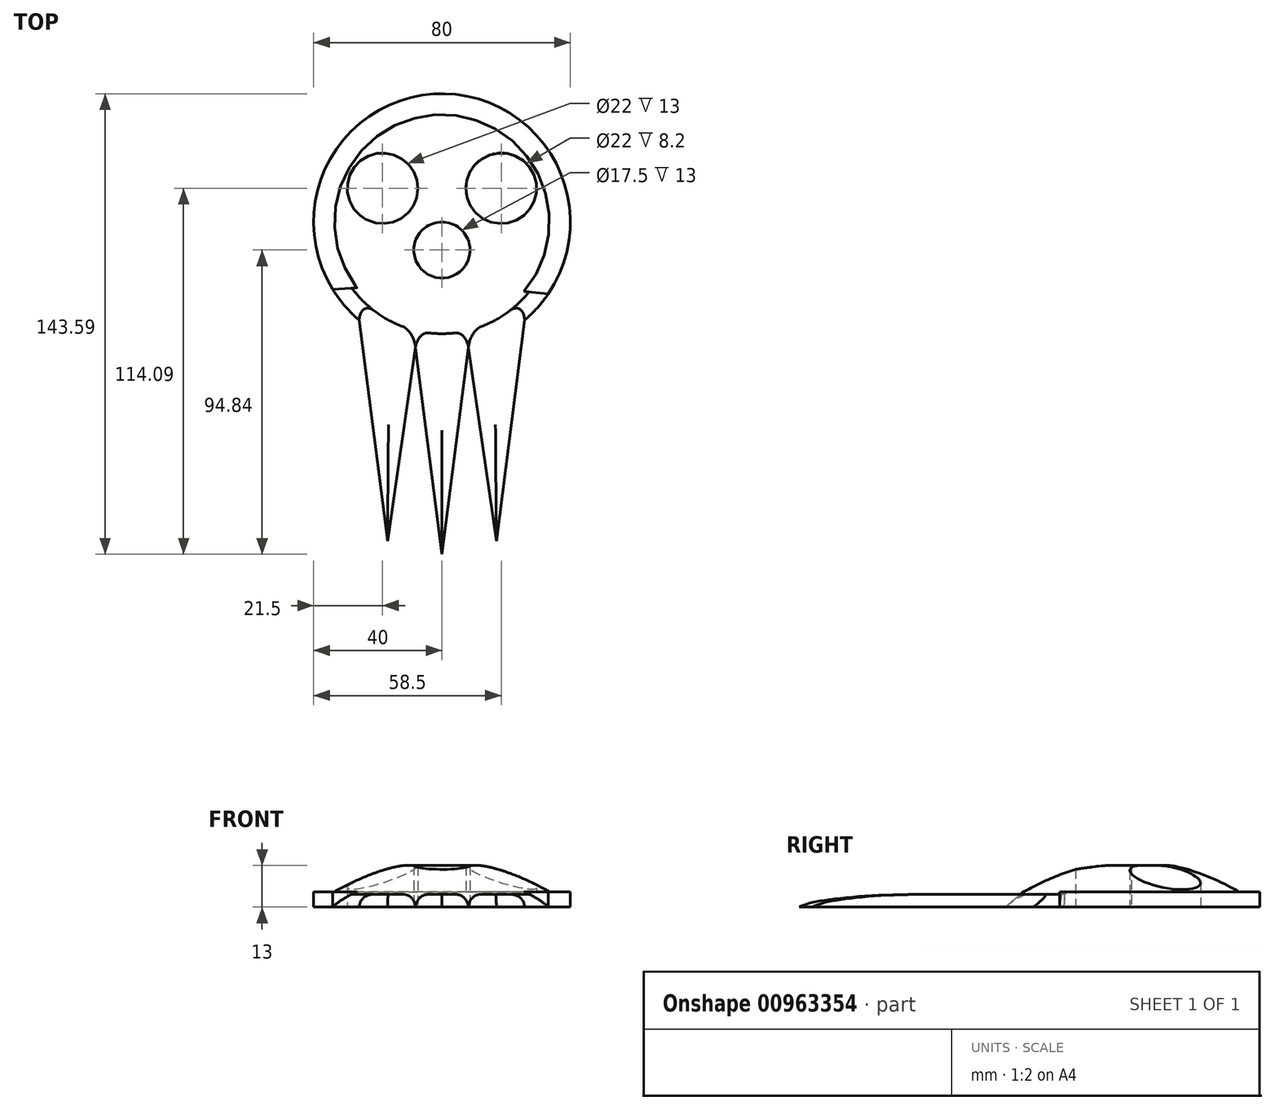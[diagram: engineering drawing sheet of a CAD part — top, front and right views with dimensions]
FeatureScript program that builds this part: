
annotation { "Feature Type Name" : "Feature", "Feature Type Description" : "" }
export const myFeature = defineFeature(function(context is Context, id is Id, definition is map)
    precondition{}
    {
        {
            var Q0;
            Q0=qCreatedBy(makeId("Top.planeOp"),FACE);
            var sketch = newSketch(context, id + "F0", { "sketchPlane" : qUnion([Q0])});
            skCircle(sketch, "E0", {"center": v(0, 0) * mm, "radius": 40 * mm});
            skLineSegment(sketch, "E1", {"start": v(0, 0) * mm, "end": v(18.5, 0) * mm});
            skLineSegment(sketch, "E2", {"start": v(18.5, 0) * mm, "end": v(18.5, 10.5) * mm});
            skCircle(sketch, "E3", {"center": v(18.5, 10.5) * mm, "radius": 11 * mm});
            skLineSegment(sketch, "E4", {"start": v(0, 0) * mm, "end": v(0, -8.75) * mm});
            skCircle(sketch, "E5", {"center": v(0, -8.75) * mm, "radius": 8.75 * mm});
            skLineSegment(sketch, "E6", {"start": v(0, 0) * mm, "end": v(0, -103.59) * mm});
            skCircle(sketch, "E7.MirrorC", {"center": v(-18.5, 10.5) * mm, "radius": 11 * mm});
            skLineSegment(sketch, "E8.MirrorCS", {"start": v(-18.5, 0) * mm, "end": v(-18.5, 10.5) * mm});
            skLineSegment(sketch, "E9.MirrorCS", {"start": v(0, 0) * mm, "end": v(-18.5, 0) * mm});
            skLineSegment(sketch, "E10", {"start": v(0, -103.59) * mm, "end": v(8.25, -39.14) * mm});
            skLineSegment(sketch, "E11", {"start": v(8.25, -39.14) * mm, "end": v(16.97, -99.51) * mm});
            skLineSegment(sketch, "E12", {"start": v(16.97, -99.51) * mm, "end": v(25.79, -30.58) * mm});
            skLineSegment(sketch, "E13.MirrorCS", {"start": v(0, -103.59) * mm, "end": v(-8.25, -39.14) * mm});
            skLineSegment(sketch, "E14.MirrorCS", {"start": v(-8.25, -39.14) * mm, "end": v(-16.97, -99.51) * mm});
            skLineSegment(sketch, "E15.MirrorCS", {"start": v(-16.97, -99.51) * mm, "end": v(-25.79, -30.58) * mm});
            skLineSegment(sketch, "E16", {"start": v(-34.05, -20.98) * mm, "end": v(0, -19.1) * mm});
            skLineSegment(sketch, "E17", {"start": v(0, -19.1) * mm, "end": v(33.14, -22.4) * mm});
            skSolve(sketch);
        }
        {
            var Q0;
            Q0=makeQuery(id+"F0.imprint","IMPRINT",FACE,{"disambiguationData":[TD([[makeQuery(id+"F0.imprint","IMPRINT",EDGE,{"derivedFrom":sQuery(id+"F0.wireOp",EDGE,"E3")}),-1.0]])]});
            var Q1;
            {var subQ2=sQuery(id+"F0.wireOp",EDGE,"CDw8CHMi-SPtq-gRNy-25xt-xmdggRBoIwYT");Q1=makeQuery(id+"F0.imprint","IMPRINT",FACE,{"disambiguationData":[TD([[makeQuery(id+"F0.imprint","IMPRINT",EDGE,{"derivedFrom":subQ2}),1.0]])]});}
            var Q2;
            {var subQ4=sQuery(id+"F0.wireOp",EDGE,"HV52Obsy-qp4e-FB5j-iO7Q-z4RWAlnaYpS9");Q2=makeQuery(id+"F0.imprint","IMPRINT",FACE,{"disambiguationData":[TD([[makeQuery(id+"F0.imprint","IMPRINT",EDGE,{"derivedFrom":subQ4}),1.0]])]});}
            var Q3;
            {var subQ0=sQuery(id+"F0.wireOp",EDGE,"E16");Q3=makeQuery(id+"F0.imprint","IMPRINT",FACE,{"disambiguationData":[TD([[makeQuery(id+"F0.imprint","IMPRINT",EDGE,{"derivedFrom":subQ0}),-1.0]])]});}
            var Q4;
            {var subQ0=sQuery(id+"F0.wireOp",EDGE,"E17");Q4=makeQuery(id+"F0.imprint","IMPRINT",FACE,{"disambiguationData":[TD([[makeQuery(id+"F0.imprint","IMPRINT",EDGE,{"derivedFrom":subQ0}),-1.0]])]});}
            extrude(context, id + "F1", {"entities" : qUnion([Q0, Q1, Q2, Q3, Q4]), "depth" : 13 * mm, "offsetDistance" : 25 * mm});
        }
        {
            var Q0;
            Q0=makeQuery(id+"F1.opExtrude","CAP_EDGE",EDGE,{"disambiguationData":[OSD([sQuery(id+"F0.wireOp",EDGE,"E0")])],"isStart":false});
            fillet(context, id + "F2", {"entities" : qUnion([Q0]), "radius" : 39 * mm, "tangentPropagation" : true, "rho" : 0.3, "crossSection" : FilletCrossSection.CONIC, "allowEdgeOverflow" : false});
        }
        {
            var Q0;
            Q0=makeQuery(id+"F0.imprint","IMPRINT",FACE,{"disambiguationData":[TD([[makeQuery(id+"F0.imprint","IMPRINT",EDGE,{"derivedFrom":sQuery(id+"F0.wireOp",EDGE,"E3")}),1.0]])]});
            var Q1;
            {var subQ0=sQuery(id+"F0.wireOp",EDGE,"E6");var subQ4=makeQuery(id+"F0.imprint","IMPRINT",VERTEX,{"derivedFrom":subQ0});Q1=makeQuery(id+"F0.imprint","IMPRINT",FACE,{"disambiguationData":[TD([[makeQuery(id+"F0.imprint","IMPRINT",EDGE,{"disambiguationData":[TD([[subQ4,1.0]])],"derivedFrom":subQ0}),1.0]])]});}
            var Q2;
            {var subQ0=sQuery(id+"F0.wireOp",EDGE,"E6");var subQ4=makeQuery(id+"F0.imprint","IMPRINT",VERTEX,{"derivedFrom":subQ0});Q2=makeQuery(id+"F0.imprint","IMPRINT",FACE,{"disambiguationData":[TD([[makeQuery(id+"F0.imprint","IMPRINT",EDGE,{"disambiguationData":[TD([[subQ4,1.0]])],"derivedFrom":subQ0}),-1.0]])]});}
            var Q3;
            Q3=makeQuery(id+"F0.imprint","IMPRINT",FACE,{"disambiguationData":[TD([[makeQuery(id+"F0.imprint","IMPRINT",EDGE,{"derivedFrom":sQuery(id+"F0.wireOp",EDGE,"E7.MirrorC")}),-1.0]])]});
            extrude(context, id + "F3", {"entities" : qUnion([Q0, Q1, Q2, Q3]), "operationType" : NewBodyOperationType.ADD, "depth" : 4.8 * mm, "offsetDistance" : 25 * mm});
        }
        {
            var Q0;
            {var subQ0=sQuery(id+"F0.wireOp",EDGE,"E14.MirrorCS");Q0=makeQuery(id+"F0.imprint","IMPRINT",FACE,{"disambiguationData":[TD([[makeQuery(id+"F0.imprint","IMPRINT",EDGE,{"derivedFrom":subQ0}),-1.0]])]});}
            var Q1;
            {var subQ0=sQuery(id+"F0.wireOp",EDGE,"E13.MirrorCS");Q1=makeQuery(id+"F0.imprint","IMPRINT",FACE,{"disambiguationData":[TD([[makeQuery(id+"F0.imprint","IMPRINT",EDGE,{"derivedFrom":subQ0}),-1.0]])]});}
            var Q2;
            {var subQ0=sQuery(id+"F0.wireOp",EDGE,"E10");Q2=makeQuery(id+"F0.imprint","IMPRINT",FACE,{"disambiguationData":[TD([[makeQuery(id+"F0.imprint","IMPRINT",EDGE,{"derivedFrom":subQ0}),1.0]])]});}
            var Q3;
            {var subQ0=sQuery(id+"F0.wireOp",EDGE,"E11");Q3=makeQuery(id+"F0.imprint","IMPRINT",FACE,{"disambiguationData":[TD([[makeQuery(id+"F0.imprint","IMPRINT",EDGE,{"derivedFrom":subQ0}),1.0]])]});}
            var Q4;
            {var subQ4=sQuery(id+"F0.wireOp",EDGE,"HV52Obsy-qp4e-FB5j-iO7Q-z4RWAlnaYpS9");Q4=makeQuery(id+"F0.imprint","IMPRINT",FACE,{"disambiguationData":[TD([[makeQuery(id+"F0.imprint","IMPRINT",EDGE,{"derivedFrom":subQ4}),1.0]])]});}
            var Q5;
            {var subQ2=sQuery(id+"F0.wireOp",EDGE,"CDw8CHMi-SPtq-gRNy-25xt-xmdggRBoIwYT");Q5=makeQuery(id+"F0.imprint","IMPRINT",FACE,{"disambiguationData":[TD([[makeQuery(id+"F0.imprint","IMPRINT",EDGE,{"derivedFrom":subQ2}),1.0]])]});}
            var Q6;
            {var subQ0=sQuery(id+"F0.wireOp",EDGE,"E17");Q6=makeQuery(id+"F0.imprint","IMPRINT",FACE,{"disambiguationData":[TD([[makeQuery(id+"F0.imprint","IMPRINT",EDGE,{"derivedFrom":subQ0}),-1.0]])]});}
            var Q7;
            {var subQ0=sQuery(id+"F0.wireOp",EDGE,"E16");Q7=makeQuery(id+"F0.imprint","IMPRINT",FACE,{"disambiguationData":[TD([[makeQuery(id+"F0.imprint","IMPRINT",EDGE,{"derivedFrom":subQ0}),-1.0]])]});}
            extrude(context, id + "F4", {"entities" : qUnion([Q0, Q1, Q2, Q3, Q4, Q5, Q6, Q7]), "operationType" : NewBodyOperationType.ADD, "depth" : 4 * mm, "offsetDistance" : 25 * mm});
        }
        {
            var Q0;
            Q0=makeQuery(id+"F4.opExtrude","CAP_EDGE",EDGE,{"disambiguationData":[OSD([sQuery(id+"F0.wireOp",EDGE,"E15.MirrorCS")])],"isStart":false});
            var Q1;
            Q1=makeQuery(id+"F4.opExtrude","CAP_EDGE",EDGE,{"disambiguationData":[OSD([sQuery(id+"F0.wireOp",EDGE,"E14.MirrorCS")])],"isStart":false});
            var Q2;
            Q2=makeQuery(id+"F4.opExtrude","CAP_EDGE",EDGE,{"disambiguationData":[OSD([sQuery(id+"F0.wireOp",EDGE,"E13.MirrorCS")])],"isStart":false});
            var Q3;
            Q3=makeQuery(id+"F4.opExtrude","CAP_EDGE",EDGE,{"disambiguationData":[OSD([sQuery(id+"F0.wireOp",EDGE,"E10")])],"isStart":false});
            var Q4;
            Q4=makeQuery(id+"F4.opExtrude","CAP_EDGE",EDGE,{"disambiguationData":[OSD([sQuery(id+"F0.wireOp",EDGE,"E11")])],"isStart":false});
            var Q5;
            Q5=makeQuery(id+"F4.opExtrude","CAP_EDGE",EDGE,{"disambiguationData":[OSD([sQuery(id+"F0.wireOp",EDGE,"E12")])],"isStart":false});
            fillet(context, id + "F5", {"entities" : qUnion([Q0, Q1, Q2, Q3, Q4, Q5]), "radius" : 5 * mm, "tangentPropagation" : true, "allowEdgeOverflow" : false});
        }
        {
            var Q0;
            {var subQ0=sQuery(id+"F0.wireOp",EDGE,"E0");Q0=makeQuery(id+"F4.opExtrude","CAP_EDGE",EDGE,{"disambiguationData":[OSD([subQ0]),TDD([makeQuery(id+"F0.imprint","IMPRINT",EDGE,{"disambiguationData":[TD([[makeQuery(id+"F0.imprint","INTERSECT",VERTEX,{"derivedFrom":[subQ0,sQuery(id+"F0.wireOp",EDGE,"E15.MirrorCS")]}),1.0]])],"derivedFrom":subQ0})])],"isStart":false});}
            var Q1;
            {var subQ0=sQuery(id+"F0.wireOp",EDGE,"E0");Q1=makeQuery(id+"F4.opExtrude","CAP_EDGE",EDGE,{"disambiguationData":[OSD([subQ0]),TDD([makeQuery(id+"F0.imprint","IMPRINT",EDGE,{"disambiguationData":[TD([[makeQuery(id+"F0.imprint","INTERSECT",VERTEX,{"derivedFrom":[subQ0,sQuery(id+"F0.wireOp",EDGE,"E12")]}),-1.0]])],"derivedFrom":subQ0})])],"isStart":false});}
            fillet(context, id + "F6", {"entities" : qUnion([Q0, Q1]), "radius" : 13 * mm, "tangentPropagation" : true, "rho" : 0.3, "crossSection" : FilletCrossSection.CONIC, "allowEdgeOverflow" : false});
        }
    });
